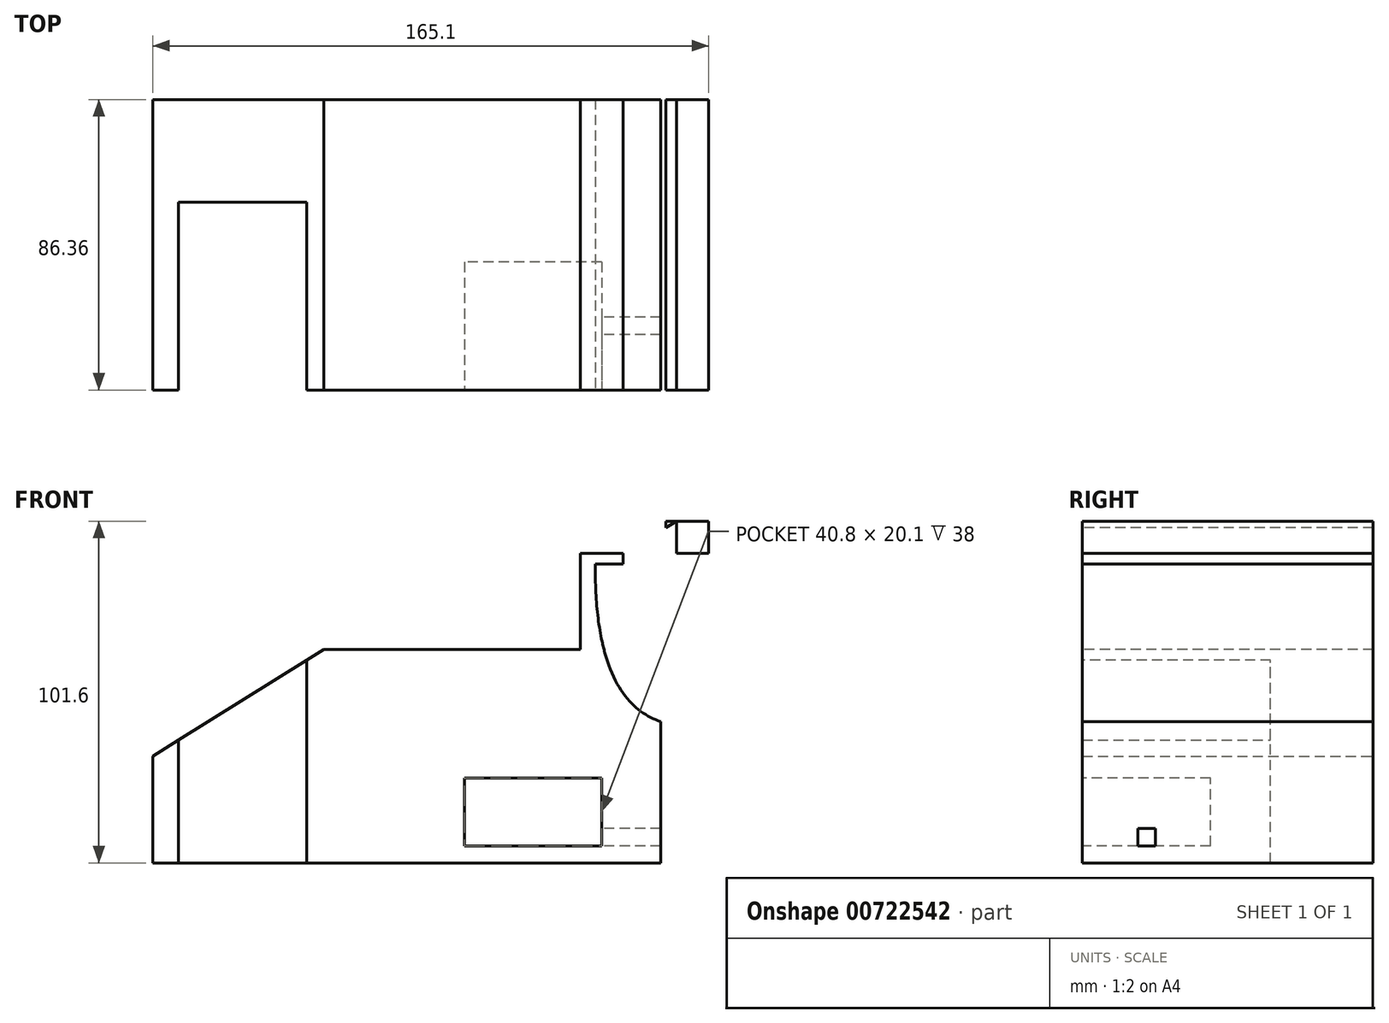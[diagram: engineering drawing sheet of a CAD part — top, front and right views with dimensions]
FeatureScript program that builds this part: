
annotation { "Feature Type Name" : "Feature", "Feature Type Description" : "" }
export const myFeature = defineFeature(function(context is Context, id is Id, definition is map)
    precondition{}
    {
        {
            var Q0;
            Q0=qCreatedBy(makeId("Top.planeOp"),FACE);
            var sketch = newSketch(context, id + "F0", { "sketchPlane" : qUnion([Q0])});
            skLineSegment(sketch, "E0.bottom", {"start": v(25.4, -38.7) * mm, "end": v(-25.4, -38.7) * mm});
            skLineSegment(sketch, "E0.top", {"start": v(25.4, 47.66) * mm, "end": v(-25.4, 47.66) * mm});
            skLineSegment(sketch, "E0.left", {"start": v(25.4, -38.7) * mm, "end": v(25.4, 47.66) * mm});
            skLineSegment(sketch, "E0.right", {"start": v(-25.4, -38.7) * mm, "end": v(-25.4, 47.66) * mm});
            skPoint(sketch, "E0.middle", {"position": v(0, 4.48) * mm});
            skSolve(sketch);
        }
        {
            var Q0;
            Q0=makeQuery(id+"F0.imprint","IMPRINT",FACE,{"disambiguationData":[TD([[makeQuery(id+"F0.imprint","IMPRINT",EDGE,{"derivedFrom":sQuery(id+"F0.wireOp",EDGE,"E0.bottom")}),-1.0]])]});
            extrude(context, id + "F1", {"entities" : qUnion([Q0]), "depth" : 63.5 * mm, "offsetDistance" : 25.4 * mm});
        }
        {
            var Q0;
            Q0=makeQuery(id+"F1.opExtrude","CAP_FACE",FACE,{"disambiguationData":[OSD([sQuery(id+"F0.wireOp",EDGE,"E0.bottom"),sQuery(id+"F0.wireOp",EDGE,"E0.top"),sQuery(id+"F0.wireOp",EDGE,"E0.left"),sQuery(id+"F0.wireOp",EDGE,"E0.right")])],"isStart":false});
            var sketch = newSketch(context, id + "F2", { "sketchPlane" : qUnion([Q0])});
            skLineSegment(sketch, "E1", {"start": v(0, 47.66) * mm, "end": v(0, -38.7) * mm});
            skLineSegment(sketch, "E2", {"start": v(-25.4, 4.48) * mm, "end": v(25.4, 4.48) * mm});
            skPoint(sketch, "E3.middle", {"position": v(0, 4.48) * mm});
            skLineSegment(sketch, "E4", {"start": v(-25.4, -38.7) * mm, "end": v(-17.78, -38.7) * mm});
            skLineSegment(sketch, "E5", {"start": v(25.4, -38.7) * mm, "end": v(20.32, -38.7) * mm});
            skLineSegment(sketch, "E6", {"start": v(20.32, -38.7) * mm, "end": v(20.32, 17.18) * mm});
            skLineSegment(sketch, "E7", {"start": v(20.32, 17.18) * mm, "end": v(-17.78, 17.18) * mm});
            skLineSegment(sketch, "E8", {"start": v(-17.78, 17.18) * mm, "end": v(-17.78, -38.7) * mm});
            skSolve(sketch);
        }
        {
            var Q0;
            {var subQ0=sQuery(id+"F2.wireOp",EDGE,"E1");var subQ1=makeQuery(id+"F1.opExtrude","CAP_EDGE",EDGE,{"disambiguationData":[OSD([sQuery(id+"F0.wireOp",EDGE,"E0.bottom")])],"isStart":false});var subQ2=makeQuery(id+"F2.imprint","INTERSECT",VERTEX,{"derivedFrom":[subQ1,subQ0]});Q0=makeQuery(id+"F2.imprint","IMPRINT",FACE,{"disambiguationData":[TD([[makeQuery(id+"F2.imprint","IMPRINT",EDGE,{"disambiguationData":[TD([[subQ2,1.0]])],"derivedFrom":subQ0}),1.0]])]});}
            var Q1;
            {var subQ0=sQuery(id+"F2.wireOp",EDGE,"E1");var subQ1=makeQuery(id+"F1.opExtrude","CAP_EDGE",EDGE,{"disambiguationData":[OSD([sQuery(id+"F0.wireOp",EDGE,"E0.bottom")])],"isStart":false});var subQ2=makeQuery(id+"F2.imprint","INTERSECT",VERTEX,{"derivedFrom":[subQ1,subQ0]});Q1=makeQuery(id+"F2.imprint","IMPRINT",FACE,{"disambiguationData":[TD([[makeQuery(id+"F2.imprint","IMPRINT",EDGE,{"disambiguationData":[TD([[subQ2,1.0]])],"derivedFrom":subQ0}),-1.0]])]});}
            var Q2;
            {var subQ0=sQuery(id+"F2.wireOp",EDGE,"E7");var subQ1=sQuery(id+"F2.wireOp",EDGE,"E1");var subQ2=makeQuery(id+"F2.imprint","INTERSECT",VERTEX,{"derivedFrom":[subQ1,subQ0]});Q2=makeQuery(id+"F2.imprint","IMPRINT",FACE,{"disambiguationData":[TD([[makeQuery(id+"F2.imprint","IMPRINT",EDGE,{"disambiguationData":[TD([[subQ2,-1.0]])],"derivedFrom":subQ1}),-1.0]])]});}
            var Q3;
            {var subQ0=sQuery(id+"F2.wireOp",EDGE,"E7");var subQ1=sQuery(id+"F2.wireOp",EDGE,"E1");var subQ2=makeQuery(id+"F2.imprint","INTERSECT",VERTEX,{"derivedFrom":[subQ1,subQ0]});Q3=makeQuery(id+"F2.imprint","IMPRINT",FACE,{"disambiguationData":[TD([[makeQuery(id+"F2.imprint","IMPRINT",EDGE,{"disambiguationData":[TD([[subQ2,-1.0]])],"derivedFrom":subQ1}),1.0]])]});}
            extrude(context, id + "F3", {"entities" : qUnion([Q0, Q1, Q2, Q3]), "operationType" : NewBodyOperationType.REMOVE, "oppositeDirection" : true, "depth" : 228.6 * mm, "offsetDistance" : 25.4 * mm});
        }
        {
            var Q0;
            Q0=makeQuery(id+"F1.opExtrude","SWEPT_FACE",FACE,{"disambiguationData":[OSD([sQuery(id+"F0.wireOp",EDGE,"E0.top")])]});
            var sketch = newSketch(context, id + "F4", { "sketchPlane" : qUnion([Q0])});
            skLineSegment(sketch, "E9", {"start": v(25.4, 0) * mm, "end": v(25.4, 31.75) * mm});
            skLineSegment(sketch, "E10", {"start": v(25.4, 31.75) * mm, "end": v(-25.4, 63.5) * mm});
            skSolve(sketch);
        }
        {
            var Q0;
            {var subQ0=sQuery(id+"F4.wireOp",EDGE,"E10");Q0=makeQuery(id+"F4.imprint","IMPRINT",FACE,{"disambiguationData":[TD([[makeQuery(id+"F4.imprint","IMPRINT",EDGE,{"derivedFrom":subQ0}),-1.0]])]});}
            extrude(context, id + "F5", {"entities" : qUnion([Q0]), "operationType" : NewBodyOperationType.REMOVE, "oppositeDirection" : true, "depth" : 228.6 * mm, "offsetDistance" : 25.4 * mm});
        }
        {
            var Q0;
            Q0=makeQuery(id+"F1.opExtrude","SWEPT_FACE",FACE,{"disambiguationData":[OSD([sQuery(id+"F0.wireOp",EDGE,"E0.left")])]});
            var sketch = newSketch(context, id + "F6", { "sketchPlane" : qUnion([Q0])});
            skLineSegment(sketch, "E11.bottom", {"start": v(-38.7, 0) * mm, "end": v(47.66, 0) * mm});
            skLineSegment(sketch, "E11.top", {"start": v(-38.7, 114.3) * mm, "end": v(47.66, 114.3) * mm});
            skLineSegment(sketch, "E11.left", {"start": v(-38.7, 0) * mm, "end": v(-38.7, 114.3) * mm});
            skLineSegment(sketch, "E11.right", {"start": v(47.66, 0) * mm, "end": v(47.66, 114.3) * mm});
            skSolve(sketch);
        }
        {
            var Q0;
            {var subQ0=sQuery(id+"F6.wireOp",EDGE,"E11.top");Q0=makeQuery(id+"F6.imprint","IMPRINT",FACE,{"disambiguationData":[TD([[makeQuery(id+"F6.imprint","IMPRINT",EDGE,{"derivedFrom":subQ0}),-1.0]])]});}
            var Q1;
            {var subQ0=sQuery(id+"F6.wireOp",EDGE,"E11.bottom");Q1=makeQuery(id+"F6.imprint","IMPRINT",FACE,{"disambiguationData":[TD([[makeQuery(id+"F6.imprint","IMPRINT",EDGE,{"derivedFrom":subQ0}),1.0]])]});}
            extrude(context, id + "F7", {"entities" : qUnion([Q0, Q1]), "operationType" : NewBodyOperationType.ADD, "depth" : 127 * mm, "offsetDistance" : 25.4 * mm});
        }
        {
            var Q0;
            {var subQ1=sQuery(id+"F0.wireOp",EDGE,"E0.left");var subQ3=sQuery(id+"F0.wireOp",EDGE,"E0.bottom");Q0=makeQuery(id+"F7.boolean.opBoolean","MERGE",FACE,{"derivedFrom":[makeQuery(id+"F3.boolean.opBoolean","SPLIT",FACE,{"disambiguationData":[TD([makeQuery(id+"F1.opExtrude","SWEPT_FACE",FACE,{"disambiguationData":[OSD([subQ1])]})])],"derivedFrom":makeQuery(id+"F1.opExtrude","SWEPT_FACE",FACE,{"disambiguationData":[OSD([subQ3])]})}),makeQuery(id+"F7.opExtrude","SWEPT_FACE",FACE,{"disambiguationData":[OSD([sQuery(id+"F6.wireOp",EDGE,"E11.left")])]})]});}
            var sketch = newSketch(context, id + "F8", { "sketchPlane" : qUnion([Q0])});
            skLineSegment(sketch, "E12", {"start": v(25.4, 63.5) * mm, "end": v(152.4, 63.5) * mm});
            skLineSegment(sketch, "E13", {"start": v(152.4, 114.3) * mm, "end": v(101.6, 114.3) * mm});
            skLineSegment(sketch, "E14", {"start": v(101.6, 114.3) * mm, "end": v(101.6, 63.5) * mm});
            skLineSegment(sketch, "E15", {"start": v(101.6, 63.5) * mm, "end": v(101.6, 88.9) * mm});
            skFitSpline(sketch, "E16", {"points": [v(101.6, 88.9) * mm, v(56.46, 63.5) * mm, v(25.4, 114.3) * mm, v(19.9, 130.64) * mm], "startDerivative": vector(-196.62, -34.97) * mm, "endDerivative": vector(-5.13, 63.21) * mm});
            skSolve(sketch);
        }
        {
            var Q0;
            {var subQ1=sQuery(id+"F0.wireOp",EDGE,"E0.left");var subQ3=sQuery(id+"F0.wireOp",EDGE,"E0.bottom");Q0=makeQuery(id+"F7.boolean.opBoolean","MERGE",FACE,{"derivedFrom":[makeQuery(id+"F3.boolean.opBoolean","SPLIT",FACE,{"disambiguationData":[TD([makeQuery(id+"F1.opExtrude","SWEPT_FACE",FACE,{"disambiguationData":[OSD([subQ1])]})])],"derivedFrom":makeQuery(id+"F1.opExtrude","SWEPT_FACE",FACE,{"disambiguationData":[OSD([subQ3])]})}),makeQuery(id+"F7.opExtrude","SWEPT_FACE",FACE,{"disambiguationData":[OSD([sQuery(id+"F6.wireOp",EDGE,"E11.left")])]})]});}
            var sketch = newSketch(context, id + "F9", { "sketchPlane" : qUnion([Q0])});
            skLineSegment(sketch, "E17", {"start": v(25.4, 63.5) * mm, "end": v(152.4, 63.5) * mm});
            skSolve(sketch);
        }
        {
            var Q0;
            Q0 = qSketchRegion(id + "F9", true);
            var Q1;
            {var subQ1=sQuery(id+"F6.wireOp",EDGE,"E11.left");var subQ2=makeQuery(id+"F7.opExtrude","CAP_EDGE",EDGE,{"disambiguationData":[OSD([subQ1])],"isStart":true});Q1=makeQuery(id+"F9.imprint","IMPRINT",FACE,{"disambiguationData":[TD([[makeQuery(id+"F9.imprint","IMPRINT",EDGE,{"derivedFrom":subQ2}),-1.0]])]});}
            extrude(context, id + "F10", {"entities" : qUnion([Q0, Q1]), "operationType" : NewBodyOperationType.REMOVE, "oppositeDirection" : true, "depth" : 228.6 * mm, "offsetDistance" : 25.4 * mm});
        }
        {
            var Q0;
            {var subQ1=sQuery(id+"F0.wireOp",EDGE,"E0.left");var subQ3=sQuery(id+"F0.wireOp",EDGE,"E0.bottom");Q0=makeQuery(id+"F7.boolean.opBoolean","MERGE",FACE,{"derivedFrom":[makeQuery(id+"F3.boolean.opBoolean","SPLIT",FACE,{"disambiguationData":[TD([makeQuery(id+"F1.opExtrude","SWEPT_FACE",FACE,{"disambiguationData":[OSD([subQ1])]})])],"derivedFrom":makeQuery(id+"F1.opExtrude","SWEPT_FACE",FACE,{"disambiguationData":[OSD([subQ3])]})}),makeQuery(id+"F7.opExtrude","SWEPT_FACE",FACE,{"disambiguationData":[OSD([sQuery(id+"F6.wireOp",EDGE,"E11.left")])]})]});}
            var sketch = newSketch(context, id + "F11", { "sketchPlane" : qUnion([Q0])});
            skLineSegment(sketch, "E18", {"start": v(152.4, 13.36) * mm, "end": v(107.95, 13.36) * mm});
            skLineSegment(sketch, "E19", {"start": v(107.95, 5.08) * mm, "end": v(107.95, 13.36) * mm});
            skLineSegment(sketch, "E20", {"start": v(107.95, 5.08) * mm, "end": v(67.15, 5.08) * mm});
            skLineSegment(sketch, "E21", {"start": v(67.15, 5.08) * mm, "end": v(67.15, 25.18) * mm});
            skLineSegment(sketch, "E22", {"start": v(67.15, 25.18) * mm, "end": v(107.95, 25.18) * mm});
            skLineSegment(sketch, "E23", {"start": v(107.95, 25.18) * mm, "end": v(107.95, 5.08) * mm});
            skSolve(sketch);
        }
        {
            var Q0;
            {var subQ1=sQuery(id+"F11.wireOp",EDGE,"E21");Q0=makeQuery(id+"F11.imprint","IMPRINT",FACE,{"disambiguationData":[TD([[makeQuery(id+"F11.imprint","IMPRINT",EDGE,{"derivedFrom":subQ1}),-1.0]])]});}
            extrude(context, id + "F12", {"entities" : qUnion([Q0]), "operationType" : NewBodyOperationType.REMOVE, "oppositeDirection" : true, "depth" : 38 * mm, "offsetDistance" : 25.4 * mm});
        }
        {
            var Q0;
            {var subQ0=sQuery(id+"F8.wireOp",EDGE,"E15");Q0=makeQuery(id+"F8.imprint","IMPRINT",FACE,{"disambiguationData":[TD([[makeQuery(id+"F8.imprint","IMPRINT",EDGE,{"derivedFrom":subQ0}),1.0]])]});}
            var Q1;
            {var subQ1=sQuery(id+"F8.wireOp",EDGE,"E13");Q1=makeQuery(id+"F8.imprint","IMPRINT",FACE,{"disambiguationData":[TD([[makeQuery(id+"F8.imprint","IMPRINT",EDGE,{"derivedFrom":subQ1}),1.0]])]});}
            extrude(context, id + "F13", {"entities" : qUnion([Q0, Q1]), "operationType" : NewBodyOperationType.ADD, "oppositeDirection" : true, "depth" : 86.36 * mm, "offsetDistance" : 25.4 * mm});
        }
        {
            var Q0;
            {var subQ0=sQuery(id+"F6.wireOp",EDGE,"E11.left");Q0=makeQuery(id+"F13.boolean.opBoolean","MERGE",FACE,{"derivedFrom":[makeQuery(id+"F7.opExtrude","CAP_FACE",FACE,{"disambiguationData":[OSD([sQuery(id+"F6.wireOp",EDGE,"E11.bottom"),sQuery(id+"F6.wireOp",EDGE,"E11.top"),subQ0,sQuery(id+"F6.wireOp",EDGE,"E11.right")])],"isStart":false}),makeQuery(id+"F13.opExtrude","SWEPT_FACE",FACE,{"disambiguationData":[OSD([subQ0])]})]});}
            var sketch = newSketch(context, id + "F14", { "sketchPlane" : qUnion([Q0])});
            skLineSegment(sketch, "E24", {"start": v(-38.7, 114.3) * mm, "end": v(-38.7, 88.9) * mm});
            skLineSegment(sketch, "E25", {"start": v(-38.7, 88.9) * mm, "end": v(47.66, 88.9) * mm});
            skLineSegment(sketch, "E26", {"start": v(47.66, 88.9) * mm, "end": v(47.66, 101.6) * mm});
            skSolve(sketch);
        }
        {
            var Q0;
            Q0=makeQuery(id+"F14.imprint","IMPRINT",FACE,{"disambiguationData":[TD([[makeQuery(id+"F14.imprint","IMPRINT",EDGE,{"derivedFrom":sQuery(id+"F14.wireOp",EDGE,"E24")}),-1.0]])]});
            extrude(context, id + "F15", {"entities" : qUnion([Q0]), "operationType" : NewBodyOperationType.REMOVE, "oppositeDirection" : true, "depth" : 101.6 * mm, "offsetDistance" : 25.4 * mm});
        }
        {
            var Q0;
            {var subQ0=sQuery(id+"F6.wireOp",EDGE,"E11.left");var subQ2=sQuery(id+"F0.wireOp",EDGE,"E0.left");var subQ4=sQuery(id+"F0.wireOp",EDGE,"E0.bottom");Q0=makeQuery(id+"F13.boolean.opBoolean","MERGE",FACE,{"derivedFrom":[makeQuery(id+"F7.boolean.opBoolean","MERGE",FACE,{"derivedFrom":[makeQuery(id+"F3.boolean.opBoolean","SPLIT",FACE,{"disambiguationData":[TD([makeQuery(id+"F1.opExtrude","SWEPT_FACE",FACE,{"disambiguationData":[OSD([subQ2])]})])],"derivedFrom":makeQuery(id+"F1.opExtrude","SWEPT_FACE",FACE,{"disambiguationData":[OSD([subQ4])]})}),makeQuery(id+"F7.opExtrude","SWEPT_FACE",FACE,{"disambiguationData":[OSD([subQ0])]})]}),makeQuery(id+"F13.opExtrude","CAP_FACE",FACE,{"disambiguationData":[OSD([subQ0,sQuery(id+"F8.wireOp",EDGE,"E12"),sQuery(id+"F8.wireOp",EDGE,"E13"),sQuery(id+"F8.wireOp",EDGE,"E14"),sQuery(id+"F8.wireOp",EDGE,"E16")])],"isStart":true})]});}
            var sketch = newSketch(context, id + "F16", { "sketchPlane" : qUnion([Q0])});
            skLineSegment(sketch, "E27", {"start": v(101.6, 88.9) * mm, "end": v(101.6, 0) * mm});
            skLineSegment(sketch, "E28", {"start": v(101.6, 0) * mm, "end": v(101.6, 44.45) * mm});
            skLineSegment(sketch, "E29", {"start": v(101.6, 44.45) * mm, "end": v(101.6, 88.9) * mm});
            skLineSegment(sketch, "E30", {"start": v(101.6, 66.68) * mm, "end": v(152.4, 66.68) * mm});
            skLineSegment(sketch, "E31", {"start": v(101.6, 88.9) * mm, "end": v(110.49, 88.9) * mm});
            skLineSegment(sketch, "E32", {"start": v(110.49, 88.9) * mm, "end": v(110.49, 0) * mm});
            skLineSegment(sketch, "E33", {"start": v(125.47, 45.06) * mm, "end": v(125.47, 0) * mm});
            skFitSpline(sketch, "E34", {"points": [v(106.04, 88.9) * mm, v(152.4, 44.45) * mm, v(157.72, 45.76) * mm], "startDerivative": vector(-2.32, -246.99) * mm, "endDerivative": vector(30.68, 18.7) * mm});
            skSolve(sketch);
        }
        {
            var Q0;
            {var subQ0=sQuery(id+"F16.wireOp",EDGE,"E34");var subQ1=sQuery(id+"F16.wireOp",EDGE,"E30");var subQ2=makeQuery(id+"F16.imprint","INTERSECT",VERTEX,{"derivedFrom":[subQ1,subQ0]});Q0=makeQuery(id+"F16.imprint","IMPRINT",FACE,{"disambiguationData":[TD([[makeQuery(id+"F16.imprint","IMPRINT",EDGE,{"disambiguationData":[TD([[subQ2,-1.0]])],"derivedFrom":subQ1}),1.0]])]});}
            var Q1;
            {var subQ0=sQuery(id+"F16.wireOp",EDGE,"E30");var subQ4=sQuery(id+"F16.wireOp",EDGE,"E32");var subQ5=makeQuery(id+"F16.imprint","INTERSECT",VERTEX,{"derivedFrom":[subQ0,subQ4]});Q1=makeQuery(id+"F16.imprint","IMPRINT",FACE,{"disambiguationData":[TD([[makeQuery(id+"F16.imprint","IMPRINT",EDGE,{"disambiguationData":[TD([[subQ5,-1.0]])],"derivedFrom":subQ0}),1.0]])]});}
            var Q2;
            {var subQ0=sQuery(id+"F16.wireOp",EDGE,"E33");var subQ6=sQuery(id+"F16.wireOp",EDGE,"E34");var subQ7=makeQuery(id+"F16.imprint","INTERSECT",VERTEX,{"derivedFrom":[subQ0,subQ6]});Q2=makeQuery(id+"F16.imprint","IMPRINT",FACE,{"disambiguationData":[TD([[makeQuery(id+"F16.imprint","IMPRINT",EDGE,{"disambiguationData":[TD([[subQ7,-1.0]])],"derivedFrom":subQ6}),-1.0]])]});}
            var Q3;
            {var subQ2=sQuery(id+"F16.wireOp",EDGE,"E32");var subQ4=sQuery(id+"F16.wireOp",EDGE,"E30");var subQ5=makeQuery(id+"F16.imprint","INTERSECT",VERTEX,{"derivedFrom":[subQ4,subQ2]});Q3=makeQuery(id+"F16.imprint","IMPRINT",FACE,{"disambiguationData":[TD([[makeQuery(id+"F16.imprint","IMPRINT",EDGE,{"disambiguationData":[TD([[subQ5,-1.0]])],"derivedFrom":subQ2}),1.0]])]});}
            var Q4;
            {var subQ0=sQuery(id+"F16.wireOp",EDGE,"E34");var subQ1=sQuery(id+"F16.wireOp",EDGE,"E30");var subQ2=makeQuery(id+"F16.imprint","INTERSECT",VERTEX,{"derivedFrom":[subQ1,subQ0]});Q4=makeQuery(id+"F16.imprint","IMPRINT",FACE,{"disambiguationData":[TD([[makeQuery(id+"F16.imprint","IMPRINT",EDGE,{"disambiguationData":[TD([[subQ2,-1.0]])],"derivedFrom":subQ1}),-1.0]])]});}
            extrude(context, id + "F17", {"entities" : qUnion([Q0, Q1, Q2, Q3, Q4]), "operationType" : NewBodyOperationType.REMOVE, "oppositeDirection" : true, "depth" : 228.6 * mm, "offsetDistance" : 25.4 * mm});
        }
        {
            var Q0;
            Q0=makeQuery(id+"F15.boolean.opBoolean","COPY",FACE,{"derivedFrom":makeQuery(id+"F15.opExtrude","SWEPT_FACE",FACE,{"disambiguationData":[OSD([sQuery(id+"F14.wireOp",EDGE,"E25")])]})});
            var sketch = newSketch(context, id + "F18", { "sketchPlane" : qUnion([Q0])});
            skLineSegment(sketch, "E35.bottom", {"start": v(101.6, 47.66) * mm, "end": v(152.4, 47.66) * mm});
            skLineSegment(sketch, "E35.top", {"start": v(101.6, -38.7) * mm, "end": v(152.4, -38.7) * mm});
            skLineSegment(sketch, "E35.left", {"start": v(101.6, 47.66) * mm, "end": v(101.6, -38.7) * mm});
            skLineSegment(sketch, "E35.right", {"start": v(152.4, 47.66) * mm, "end": v(152.4, -38.7) * mm});
            skSolve(sketch);
        }
        {
            var Q0;
            {var subQ2=sQuery(id+"F18.wireOp",EDGE,"E35.right");Q0=makeQuery(id+"F18.imprint","IMPRINT",FACE,{"disambiguationData":[TD([[makeQuery(id+"F18.imprint","IMPRINT",EDGE,{"derivedFrom":subQ2}),-1.0]])]});}
            var Q1;
            {var subQ0=sQuery(id+"F18.wireOp",EDGE,"E35.left");Q1=makeQuery(id+"F18.imprint","IMPRINT",FACE,{"disambiguationData":[TD([[makeQuery(id+"F18.imprint","IMPRINT",EDGE,{"derivedFrom":subQ0}),1.0]])]});}
            extrude(context, id + "F19", {"entities" : qUnion([Q0, Q1]), "operationType" : NewBodyOperationType.ADD, "depth" : 12.7 * mm, "offsetDistance" : 25.4 * mm});
        }
        {
            var Q0;
            {var subQ0=sQuery(id+"F6.wireOp",EDGE,"E11.left");var subQ2=sQuery(id+"F0.wireOp",EDGE,"E0.left");var subQ4=sQuery(id+"F0.wireOp",EDGE,"E0.bottom");Q0=makeQuery(id+"F19.boolean.opBoolean","MERGE",FACE,{"derivedFrom":[makeQuery(id+"F13.boolean.opBoolean","MERGE",FACE,{"derivedFrom":[makeQuery(id+"F7.boolean.opBoolean","MERGE",FACE,{"derivedFrom":[makeQuery(id+"F3.boolean.opBoolean","SPLIT",FACE,{"disambiguationData":[TD([makeQuery(id+"F1.opExtrude","SWEPT_FACE",FACE,{"disambiguationData":[OSD([subQ2])]})])],"derivedFrom":makeQuery(id+"F1.opExtrude","SWEPT_FACE",FACE,{"disambiguationData":[OSD([subQ4])]})}),makeQuery(id+"F7.opExtrude","SWEPT_FACE",FACE,{"disambiguationData":[OSD([subQ0])]})]}),makeQuery(id+"F13.opExtrude","CAP_FACE",FACE,{"disambiguationData":[OSD([subQ0,sQuery(id+"F8.wireOp",EDGE,"E12"),sQuery(id+"F8.wireOp",EDGE,"E13"),sQuery(id+"F8.wireOp",EDGE,"E14"),sQuery(id+"F8.wireOp",EDGE,"E16")])],"isStart":true})]}),makeQuery(id+"F19.opExtrude","SWEPT_FACE",FACE,{"disambiguationData":[OSD([sQuery(id+"F18.wireOp",EDGE,"E35.top")])]})]});}
            var sketch = newSketch(context, id + "F20", { "sketchPlane" : qUnion([Q0])});
            skLineSegment(sketch, "E36", {"start": v(152.4, 101.6) * mm, "end": v(152.4, 88.9) * mm});
            skLineSegment(sketch, "E37", {"start": v(152.4, 88.9) * mm, "end": v(152.4, 95.25) * mm});
            skLineSegment(sketch, "E38", {"start": v(152.4, 95.25) * mm, "end": v(152.4, 92.08) * mm});
            skLineSegment(sketch, "E39", {"start": v(152.4, 92.08) * mm, "end": v(101.6, 92.08) * mm});
            skLineSegment(sketch, "E40", {"start": v(127, 101.6) * mm, "end": v(127, 88.9) * mm});
            skPoint(sketch, "E40.endSnap0", {"position": v(127, 92.08) * mm});
            skLineSegment(sketch, "E41", {"start": v(101.6, 101.6) * mm, "end": v(127, 101.6) * mm});
            skLineSegment(sketch, "E42", {"start": v(114.3, 101.6) * mm, "end": v(114.3, 88.9) * mm});
            skLineSegment(sketch, "E43", {"start": v(152.4, 101.6) * mm, "end": v(127, 101.6) * mm});
            skLineSegment(sketch, "E44", {"start": v(139.7, 101.6) * mm, "end": v(139.7, 88.9) * mm});
            skLineSegment(sketch, "E45", {"start": v(139.7, 88.9) * mm, "end": v(139.7, 101.6) * mm});
            skLineSegment(sketch, "E46", {"start": v(127, 101.6) * mm, "end": v(139.7, 101.6) * mm});
            skLineSegment(sketch, "E47", {"start": v(133.35, 101.6) * mm, "end": v(133.35, 88.9) * mm});
            skLineSegment(sketch, "E48", {"start": v(133.35, 88.9) * mm, "end": v(133.35, 101.6) * mm});
            skLineSegment(sketch, "E49", {"start": v(127, 101.6) * mm, "end": v(133.35, 101.6) * mm});
            skLineSegment(sketch, "E50", {"start": v(130.17, 101.6) * mm, "end": v(130.17, 88.9) * mm});
            skLineSegment(sketch, "E51", {"start": v(130.17, 101.6) * mm, "end": v(114.3, 101.6) * mm});
            skLineSegment(sketch, "E52", {"start": v(114.3, 92.08) * mm, "end": v(130.17, 101.6) * mm});
            skSolve(sketch);
        }
        {
            var Q0;
            {var subQ5=sQuery(id+"F20.wireOp",EDGE,"E41");Q0=makeQuery(id+"F20.imprint","IMPRINT",FACE,{"disambiguationData":[TD([[makeQuery(id+"F20.imprint","IMPRINT",EDGE,{"derivedFrom":subQ5}),-1.0]])]});}
            var Q1;
            {var subQ0=sQuery(id+"F20.wireOp",EDGE,"E51");var subQ1=sQuery(id+"F20.wireOp",EDGE,"E40");var subQ2=makeQuery(id+"F20.imprint","INTERSECT",VERTEX,{"derivedFrom":[subQ1,subQ0]});Q1=makeQuery(id+"F20.imprint","IMPRINT",FACE,{"disambiguationData":[TD([[makeQuery(id+"F20.imprint","IMPRINT",EDGE,{"disambiguationData":[TD([[subQ2,-1.0]])],"derivedFrom":subQ1}),-1.0]])]});}
            var Q2;
            {var subQ0=sQuery(id+"F20.wireOp",EDGE,"E51");var subQ1=sQuery(id+"F20.wireOp",EDGE,"E40");var subQ2=makeQuery(id+"F20.imprint","INTERSECT",VERTEX,{"derivedFrom":[subQ1,subQ0]});Q2=makeQuery(id+"F20.imprint","IMPRINT",FACE,{"disambiguationData":[TD([[makeQuery(id+"F20.imprint","IMPRINT",EDGE,{"disambiguationData":[TD([[subQ2,-1.0]])],"derivedFrom":subQ1}),1.0]])]});}
            var Q3;
            {var subQ5=sQuery(id+"F20.wireOp",EDGE,"E49");Q3=makeQuery(id+"F20.imprint","IMPRINT",FACE,{"disambiguationData":[TD([[makeQuery(id+"F20.imprint","IMPRINT",EDGE,{"derivedFrom":subQ5}),-1.0]])]});}
            var Q4;
            {var subQ5=sQuery(id+"F20.wireOp",EDGE,"E46");Q4=makeQuery(id+"F20.imprint","IMPRINT",FACE,{"disambiguationData":[TD([[makeQuery(id+"F20.imprint","IMPRINT",EDGE,{"derivedFrom":subQ5}),-1.0]])]});}
            var Q5;
            {var subQ0=sQuery(id+"F20.wireOp",EDGE,"E48");var subQ1=sQuery(id+"F20.wireOp",EDGE,"E39");var subQ2=makeQuery(id+"F20.imprint","INTERSECT",VERTEX,{"derivedFrom":[subQ1,subQ0]});Q5=makeQuery(id+"F20.imprint","IMPRINT",FACE,{"disambiguationData":[TD([[makeQuery(id+"F20.imprint","IMPRINT",EDGE,{"disambiguationData":[TD([[subQ2,-1.0]])],"derivedFrom":subQ1}),1.0]])]});}
            var Q6;
            {var subQ0=sQuery(id+"F20.wireOp",EDGE,"E45");var subQ1=sQuery(id+"F20.wireOp",EDGE,"E39");var subQ2=makeQuery(id+"F20.imprint","INTERSECT",VERTEX,{"derivedFrom":[subQ1,subQ0]});Q6=makeQuery(id+"F20.imprint","IMPRINT",FACE,{"disambiguationData":[TD([[makeQuery(id+"F20.imprint","IMPRINT",EDGE,{"disambiguationData":[TD([[subQ2,-1.0]])],"derivedFrom":subQ1}),1.0]])]});}
            var Q7;
            Q7=makeQuery(id+"F20.imprint","IMPRINT",FACE,{"disambiguationData":[TD([[makeQuery(id+"F20.imprint","IMPRINT",EDGE,{"derivedFrom":sQuery(id+"F20.wireOp",EDGE,"E36")}),-1.0]])]});
            var Q8;
            {var subQ0=sQuery(id+"F20.wireOp",EDGE,"E37");Q8=makeQuery(id+"F20.imprint","IMPRINT",FACE,{"disambiguationData":[TD([[makeQuery(id+"F20.imprint","IMPRINT",EDGE,{"derivedFrom":subQ0}),-1.0]])]});}
            extrude(context, id + "F21", {"entities" : qUnion([Q0, Q1, Q2, Q3, Q4, Q5, Q6, Q7, Q8]), "operationType" : NewBodyOperationType.REMOVE, "oppositeDirection" : true, "depth" : 228.6 * mm, "offsetDistance" : 25.4 * mm});
        }
        {
            var Q0;
            {var subQ0=sQuery(id+"F6.wireOp",EDGE,"E11.left");var subQ2=sQuery(id+"F0.wireOp",EDGE,"E0.left");var subQ4=sQuery(id+"F0.wireOp",EDGE,"E0.bottom");Q0=makeQuery(id+"F19.boolean.opBoolean","MERGE",FACE,{"derivedFrom":[makeQuery(id+"F13.boolean.opBoolean","MERGE",FACE,{"derivedFrom":[makeQuery(id+"F7.boolean.opBoolean","MERGE",FACE,{"derivedFrom":[makeQuery(id+"F3.boolean.opBoolean","SPLIT",FACE,{"disambiguationData":[TD([makeQuery(id+"F1.opExtrude","SWEPT_FACE",FACE,{"disambiguationData":[OSD([subQ2])]})])],"derivedFrom":makeQuery(id+"F1.opExtrude","SWEPT_FACE",FACE,{"disambiguationData":[OSD([subQ4])]})}),makeQuery(id+"F7.opExtrude","SWEPT_FACE",FACE,{"disambiguationData":[OSD([subQ0])]})]}),makeQuery(id+"F13.opExtrude","CAP_FACE",FACE,{"disambiguationData":[OSD([subQ0,sQuery(id+"F8.wireOp",EDGE,"E12"),sQuery(id+"F8.wireOp",EDGE,"E13"),sQuery(id+"F8.wireOp",EDGE,"E14"),sQuery(id+"F8.wireOp",EDGE,"E16")])],"isStart":true})]}),makeQuery(id+"F19.opExtrude","SWEPT_FACE",FACE,{"disambiguationData":[OSD([sQuery(id+"F18.wireOp",EDGE,"E35.top")])]})]});}
            var sketch = newSketch(context, id + "F22", { "sketchPlane" : qUnion([Q0])});
            skLineSegment(sketch, "E53", {"start": v(114.3, 92.08) * mm, "end": v(114.3, 88.9) * mm});
            skLineSegment(sketch, "E54", {"start": v(114.3, 88.9) * mm, "end": v(130.17, 88.9) * mm});
            skLineSegment(sketch, "E55", {"start": v(130.17, 88.9) * mm, "end": v(130.17, 101.6) * mm});
            skLineSegment(sketch, "E56", {"start": v(130.17, 101.6) * mm, "end": v(130.17, 92.08) * mm});
            skLineSegment(sketch, "E57", {"start": v(130.17, 92.08) * mm, "end": v(114.3, 92.08) * mm});
            skLineSegment(sketch, "E58", {"start": v(122.24, 92.08) * mm, "end": v(130.17, 88.9) * mm});
            skLineSegment(sketch, "E59", {"start": v(122.24, 92.08) * mm, "end": v(114.3, 88.9) * mm});
            skSolve(sketch);
        }
        {
            var Q0;
            Q0=makeQuery(id+"F22.imprint","IMPRINT",FACE,{"disambiguationData":[TD([[makeQuery(id+"F22.imprint","IMPRINT",EDGE,{"derivedFrom":sQuery(id+"F22.wireOp",EDGE,"E54")}),1.0]])]});
            extrude(context, id + "F23", {"entities" : qUnion([Q0]), "operationType" : NewBodyOperationType.REMOVE, "oppositeDirection" : true, "depth" : 228.6 * mm, "offsetDistance" : 25.4 * mm});
        }
        {
            var Q0;
            Q0=makeQuery(id+"F12.boolean.opBoolean","COPY",FACE,{"derivedFrom":makeQuery(id+"F12.opExtrude","SWEPT_FACE",FACE,{"disambiguationData":[OSD([sQuery(id+"F11.wireOp",EDGE,"E23")])]})});
            var sketch = newSketch(context, id + "F24", { "sketchPlane" : qUnion([Q0])});
            skLineSegment(sketch, "E60.bottom", {"start": v(38.7, 25.18) * mm, "end": v(0.7, 25.18) * mm});
            skLineSegment(sketch, "E60.top", {"start": v(38.7, 5.08) * mm, "end": v(0.7, 5.08) * mm});
            skLineSegment(sketch, "E60.left", {"start": v(38.7, 25.18) * mm, "end": v(38.7, 5.08) * mm});
            skLineSegment(sketch, "E60.right", {"start": v(0.7, 25.18) * mm, "end": v(0.7, 5.08) * mm});
            skLineSegment(sketch, "E61", {"start": v(0.7, 5.08) * mm, "end": v(19.7, 5.08) * mm});
            skLineSegment(sketch, "E62", {"start": v(19.7, 5.08) * mm, "end": v(38.7, 5.08) * mm});
            skLineSegment(sketch, "E63", {"start": v(29.2, 5.08) * mm, "end": v(38.7, 5.08) * mm});
            skLineSegment(sketch, "E64", {"start": v(0.7, 5.08) * mm, "end": v(10.2, 5.08) * mm});
            skLineSegment(sketch, "E65", {"start": v(10.2, 5.08) * mm, "end": v(19.7, 5.08) * mm});
            skLineSegment(sketch, "E66", {"start": v(14.95, 5.08) * mm, "end": v(19.7, 5.08) * mm});
            skLineSegment(sketch, "E67", {"start": v(19.7, 5.08) * mm, "end": v(29.2, 5.08) * mm});
            skLineSegment(sketch, "E68", {"start": v(24.45, 5.08) * mm, "end": v(19.7, 5.08) * mm});
            skLineSegment(sketch, "E69", {"start": v(19.7, 5.08) * mm, "end": v(17.32, 5.08) * mm});
            skLineSegment(sketch, "E70", {"start": v(17.32, 5.08) * mm, "end": v(19.7, 5.08) * mm});
            skLineSegment(sketch, "E71", {"start": v(19.7, 5.08) * mm, "end": v(22.07, 5.08) * mm});
            skPoint(sketch, "E72.middle", {"position": v(19.7, 5.08) * mm});
            skLineSegment(sketch, "E73", {"start": v(19.7, 5.08) * mm, "end": v(22.3, 5.08) * mm});
            skLineSegment(sketch, "E74", {"start": v(22.3, 5.08) * mm, "end": v(17.1, 5.08) * mm});
            skLineSegment(sketch, "E75", {"start": v(22.3, 5.08) * mm, "end": v(22.3, 10.28) * mm});
            skLineSegment(sketch, "E76", {"start": v(17.1, 5.08) * mm, "end": v(17.1, 10.28) * mm});
            skLineSegment(sketch, "E77", {"start": v(17.1, 10.28) * mm, "end": v(22.3, 10.28) * mm});
            skSolve(sketch);
        }
        {
            var Q0;
            {var subQ0=sQuery(id+"F24.wireOp",EDGE,"E75");Q0=makeQuery(id+"F24.imprint","IMPRINT",FACE,{"disambiguationData":[TD([[makeQuery(id+"F24.imprint","IMPRINT",EDGE,{"derivedFrom":subQ0}),1.0]])]});}
            extrude(context, id + "F25", {"entities" : qUnion([Q0]), "operationType" : NewBodyOperationType.REMOVE, "oppositeDirection" : true, "depth" : 59.69 * mm, "offsetDistance" : 25.4 * mm});
        }
    });
